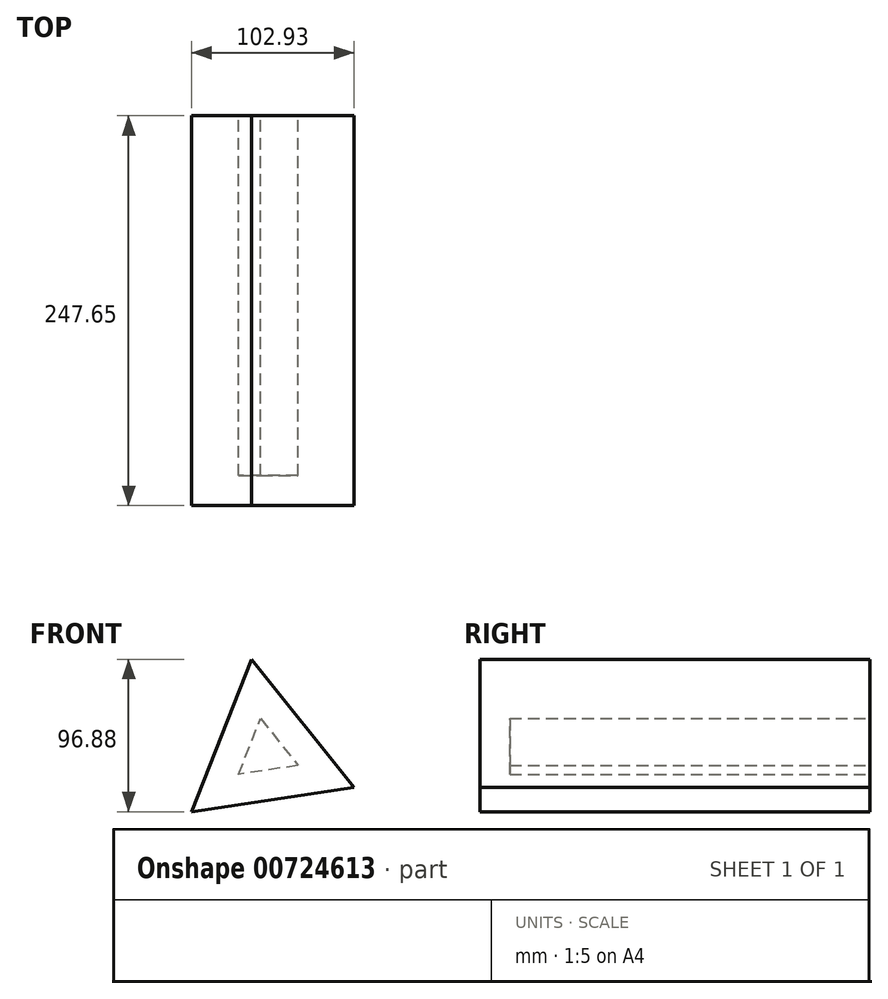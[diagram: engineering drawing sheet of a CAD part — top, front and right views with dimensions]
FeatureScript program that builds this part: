
annotation { "Feature Type Name" : "Feature", "Feature Type Description" : "" }
export const myFeature = defineFeature(function(context is Context, id is Id, definition is map)
    precondition{}
    {
        {
            var Q0;
            Q0=qCreatedBy(makeId("Front.planeOp"),FACE);
            var sketch = newSketch(context, id + "F0", { "sketchPlane" : qUnion([Q0])});
            skCircle(sketch, "E0.cCircle", {"center": v(0, 0) * mm, "radius": 11 * mm, "construction": true});
            skLineSegment(sketch, "E0.0", {"start": v(-3.27, 21.75) * mm, "end": v(20.47, -8.05) * mm});
            skLineSegment(sketch, "E0.1", {"start": v(20.47, -8.05) * mm, "end": v(-17.2, -13.7) * mm});
            skLineSegment(sketch, "E0.2", {"start": v(-17.2, -13.7) * mm, "end": v(-3.27, 21.75) * mm});
            skPoint(sketch, "E0.0.midPoint", {"position": v(8.6, 6.85) * mm});
            skSolve(sketch);
        }
        {
            var Q0;
            Q0=makeQuery(id+"F0.imprint","IMPRINT",FACE,{"disambiguationData":[TD([[makeQuery(id+"F0.imprint","IMPRINT",EDGE,{"derivedFrom":sQuery(id+"F0.wireOp",EDGE,"E0.0")}),-1.0]])]});
            extrude(context, id + "F1", {"entities" : qUnion([Q0]), "depth" : 228.6 * mm, "offsetDistance" : 25.4 * mm});
        }
        {
            var Q0;
            Q0=makeQuery(id+"F1.opExtrude","CAP_FACE",FACE,{"disambiguationData":[OSD([sQuery(id+"F0.wireOp",EDGE,"E0.0"),sQuery(id+"F0.wireOp",EDGE,"E0.1"),sQuery(id+"F0.wireOp",EDGE,"E0.2")])],"isStart":true});
            shell(context, id + "F2", {"entities" : qUnion([Q0]), "thickness" : 19.05 * mm, "oppositeDirection" : true});
        }
    });
